FCSTD DOCUMENT  (FreeCAD 0.18R16110 (Git))
Label: Trapezoidal_thread_480
License: CreativeCommons Attribution-ShareAlike
LicenseURL: http://creativecommons.org/licenses/by-sa/4.0/
objects: Sketcher::SketchObject×1, Part::Helix×1, Part::Sweep×1, Part::Cylinder×1, Part::MultiFuse×1
note: 5 computed .brp shape members not serialized (recipe doc carries the construction recipe); baked Part::Feature solids carry a one-line shape summary decoded from their .brp

FEATURE [Sketcher::SketchObject] Sketch
  MapMode = 5
  sketch-geometry (9):
    g0: Circle [constr] CenterX=0 CenterY=0 CenterZ=0 NormalX=0 NormalY=0 NormalZ=1 AngleXU=0 Radius=3.95
    g1: LineSegment StartX=-3.90416 StartY=0.6 StartZ=0 EndX=-3.90416 EndY=-0.6 EndZ=0
    g2: LineSegment StartX=-3.90416 StartY=0.6 StartZ=0 EndX=-0.6 EndY=3.90416 EndZ=0
    g3: LineSegment StartX=-0.6 StartY=3.90416 StartZ=0 EndX=0.6 EndY=3.90416 EndZ=0
    g4: LineSegment StartX=0.6 StartY=3.90416 StartZ=0 EndX=3.90416 EndY=0.6 EndZ=0
    g5: LineSegment StartX=3.90416 StartY=0.6 StartZ=0 EndX=3.90416 EndY=-0.6 EndZ=0
    g6: LineSegment StartX=3.90416 StartY=-0.6 StartZ=0 EndX=0.6 EndY=-3.90416 EndZ=0
    g7: LineSegment StartX=0.6 StartY=-3.90416 StartZ=0 EndX=-0.6 EndY=-3.90416 EndZ=0
    g8: LineSegment StartX=-0.6 StartY=-3.90416 StartZ=0 EndX=-3.90416 EndY=-0.6 EndZ=0
  constraints (29):
    c: Coincident(g0,g-1)
    c: Radius(g0) = 3.95
    c: PointOnObject(g1,g0)
    c: PointOnObject(g1,g0)
    c: Vertical(g1)
    c: Coincident(g2,g1)
    c: PointOnObject(g2,g0)
    c: Coincident(g3,g2)
    c: PointOnObject(g3,g0)
    c: Horizontal(g3)
    c: Coincident(g3,g4)
    c: PointOnObject(g4,g0)
    c: Coincident(g4,g5)
    c: PointOnObject(g5,g0)
    c: Vertical(g5)
    c: Coincident(g5,g6)
    c: PointOnObject(g6,g0)
    c: Coincident(g6,g7)
    c: PointOnObject(g7,g0)
    c: Horizontal(g7)
    c: Coincident(g7,g8)
    c: Coincident(g8,g1)
    c: Equal(g3,g5)
    c: Equal(g5,g7)
    c: Equal(g7,g1)
    c: Equal(g2,g4)
    c: Equal(g4,g6)
    c: Equal(g6,g8)
    c: DistanceY(g5,g5) = 1.2
FEATURE [Part::Helix] Helix
  Angle = 0
  AttacherType = Attacher::AttachEngine3D
  Height = 480
  LocalCoord = 0
  Pitch = 8
  Radius = 2
  Style = 1
FEATURE [Part::Sweep] Sweep
  Frenet = true
  Sections = -> [Sketch]
  Solid = true
  Spine = -> Helix
  Transition = 1
FEATURE [Part::Cylinder] Cylinder
  Angle = 360
  AttacherType = Attacher::AttachEngine3D
  Height = 140
  Radius = 3.3
FEATURE [Part::MultiFuse] Fusion
  Refine = true
  Shapes = -> [Cylinder,Sweep]
